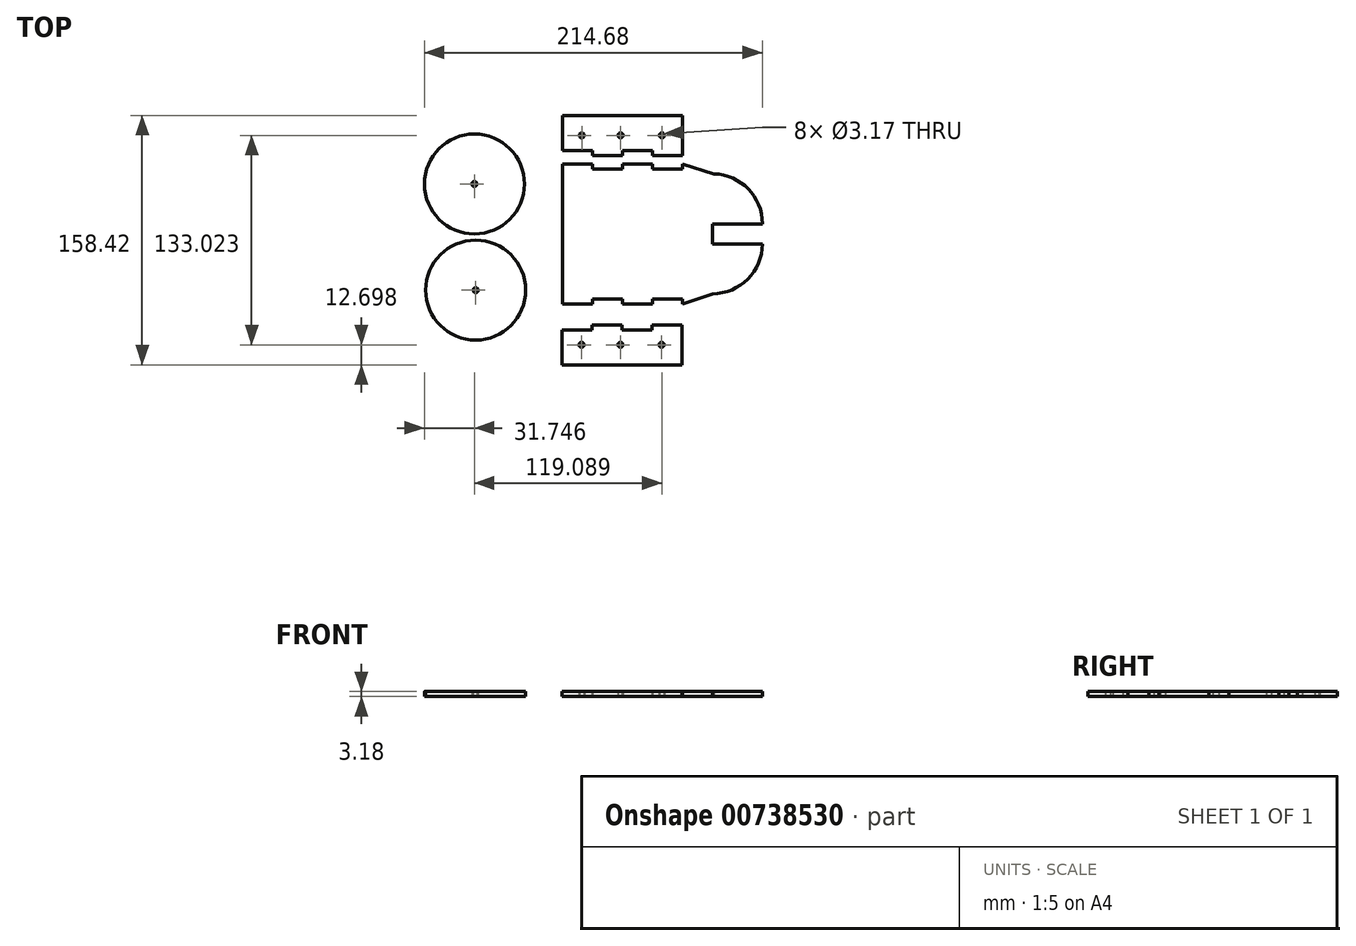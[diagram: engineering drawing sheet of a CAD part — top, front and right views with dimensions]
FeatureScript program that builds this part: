
annotation { "Feature Type Name" : "Feature", "Feature Type Description" : "" }
export const myFeature = defineFeature(function(context is Context, id is Id, definition is map)
    precondition{}
    {
        {
            var Q0;
            Q0=qCreatedBy(makeId("Top.planeOp"),FACE);
            var sketch = newSketch(context, id + "F0", { "sketchPlane" : qUnion([Q0])});
            skLineSegment(sketch, "E0.bottom", {"start": v(0, 0) * mm, "end": v(19.05, 0) * mm});
            skLineSegment(sketch, "E0.top", {"start": v(0, 88.9) * mm, "end": v(19.05, 88.9) * mm});
            skLineSegment(sketch, "E0.left", {"start": v(0, 0) * mm, "end": v(0, 88.9) * mm});
            skLineSegment(sketch, "E1.top", {"start": v(19.05, 85.73) * mm, "end": v(38.1, 85.73) * mm});
            skLineSegment(sketch, "E1.left", {"start": v(19.05, 88.9) * mm, "end": v(19.05, 85.73) * mm});
            skLineSegment(sketch, "E1.right", {"start": v(38.1, 88.9) * mm, "end": v(38.1, 85.73) * mm});
            skLineSegment(sketch, "E2.top", {"start": v(57.15, 85.73) * mm, "end": v(76.2, 85.73) * mm});
            skLineSegment(sketch, "E2.left", {"start": v(57.15, 88.9) * mm, "end": v(57.15, 85.73) * mm});
            skLineSegment(sketch, "E2.right", {"start": v(76.2, 88.9) * mm, "end": v(76.2, 85.73) * mm});
            skLineSegment(sketch, "E3.top", {"start": v(19.05, 3.18) * mm, "end": v(38.1, 3.18) * mm});
            skLineSegment(sketch, "E3.left", {"start": v(19.05, 0) * mm, "end": v(19.05, 3.18) * mm});
            skLineSegment(sketch, "E3.right", {"start": v(38.1, 0) * mm, "end": v(38.1, 3.18) * mm});
            skLineSegment(sketch, "E4.top", {"start": v(57.15, 3.18) * mm, "end": v(76.2, 3.18) * mm});
            skLineSegment(sketch, "E4.left", {"start": v(57.15, 0) * mm, "end": v(57.15, 3.18) * mm});
            skLineSegment(sketch, "E4.right", {"start": v(76.2, 0) * mm, "end": v(76.2, 3.18) * mm});
            skLineSegment(sketch, "E5.bottom", {"start": v(19.05, 94.26) * mm, "end": v(38.1, 94.26) * mm});
            skLineSegment(sketch, "E5.top", {"start": v(0, 119.66) * mm, "end": v(50.8, 119.66) * mm});
            skLineSegment(sketch, "E5.left", {"start": v(0, 97.44) * mm, "end": v(0, 119.66) * mm});
            skLineSegment(sketch, "E5.right", {"start": v(76.2, 123.98) * mm, "end": v(76.2, 123.98) * mm});
            skLineSegment(sketch, "E6.top", {"start": v(0, 97.44) * mm, "end": v(19.05, 97.44) * mm});
            skLineSegment(sketch, "E6.right", {"start": v(19.05, 94.26) * mm, "end": v(19.05, 97.44) * mm});
            skLineSegment(sketch, "E7.top", {"start": v(38.1, 97.44) * mm, "end": v(57.15, 97.44) * mm});
            skLineSegment(sketch, "E7.left", {"start": v(38.1, 94.26) * mm, "end": v(38.1, 97.44) * mm});
            skLineSegment(sketch, "E7.right", {"start": v(57.15, 94.26) * mm, "end": v(57.15, 97.44) * mm});
            skLineSegment(sketch, "E8.trimOffspring", {"start": v(57.15, 94.26) * mm, "end": v(76.2, 94.26) * mm});
            skPoint(sketch, "E9.orphan", {"position": v(0, 94.26) * mm});
            skLineSegment(sketch, "E10.trimOffspring", {"start": v(38.1, 88.9) * mm, "end": v(57.15, 88.9) * mm});
            skLineSegment(sketch, "E11.trimOffspring", {"start": v(38.1, 0) * mm, "end": v(57.15, 0) * mm});
            skLineSegment(sketch, "E12.bottom", {"start": v(127, 50.8) * mm, "end": v(95.25, 50.8) * mm});
            skLineSegment(sketch, "E12.top", {"start": v(127, 38.1) * mm, "end": v(95.25, 38.1) * mm});
            skLineSegment(sketch, "E12.right", {"start": v(95.25, 50.8) * mm, "end": v(95.25, 38.1) * mm});
            skPoint(sketch, "E13.1.internal.orphan", {"position": v(115.41, 11.02) * mm});
            skPoint(sketch, "E14.1.internal.orphan", {"position": v(115.41, 74.92) * mm});
            skArc(sketch, "E15", {"start": v(127, 50.8) * mm, "mid": v(118.02, 72.93) * mm, "end": v(96.15, 82.54) * mm});
            skArc(sketch, "E16", {"start": v(127, 38.1) * mm, "mid": v(117.7, 15.65) * mm, "end": v(95.25, 6.35) * mm});
            skLineSegment(sketch, "E17", {"start": v(76.2, 0) * mm, "end": v(95.25, 6.35) * mm});
            skLineSegment(sketch, "E18", {"start": v(96.15, 82.54) * mm, "end": v(76.2, 88.9) * mm});
            skPoint(sketch, "E19.visualSharp", {"position": v(76.2, 119.66) * mm});
            skCircle(sketch, "E20", {"center": v(12.27, 106.96) * mm, "radius": 1.59 * mm});
            skCircle(sketch, "E21", {"center": v(36.96, 106.96) * mm, "radius": 1.59 * mm});
            skCircle(sketch, "E22", {"center": v(63.15, 106.96) * mm, "radius": 1.59 * mm});
            skLineSegment(sketch, "E23", {"start": v(50.8, 119.66) * mm, "end": v(76.2, 119.66) * mm});
            skLineSegment(sketch, "E24", {"start": v(76.2, 119.66) * mm, "end": v(76.2, 94.26) * mm});
            skCircle(sketch, "E25", {"center": v(-55.93, 76.1) * mm, "radius": 31.75 * mm});
            skCircle(sketch, "E26", {"center": v(-55.93, 76.1) * mm, "radius": 1.59 * mm});
            skCircle(sketch, "E27", {"center": v(-55.09, 8.68) * mm, "radius": 31.75 * mm});
            skCircle(sketch, "E28", {"center": v(-55.09, 8.68) * mm, "radius": 1.59 * mm});
            skLineSegment(sketch, "E29.left", {"start": v(-0.16, -16.54) * mm, "end": v(-0.16, -38.76) * mm});
            skPoint(sketch, "E30.orphan", {"position": v(-0.16, -13.36) * mm});
            skLineSegment(sketch, "E31.MirrorCS", {"start": v(18.9, -13.36) * mm, "end": v(18.9, -16.54) * mm});
            skLineSegment(sketch, "E32.MirrorCS", {"start": v(57, -13.36) * mm, "end": v(57, -16.54) * mm});
            skLineSegment(sketch, "E33.MirrorCS", {"start": v(37.94, -13.36) * mm, "end": v(37.94, -16.54) * mm});
            skCircle(sketch, "E34.MirrorC", {"center": v(63, -26.06) * mm, "radius": 1.59 * mm});
            skLineSegment(sketch, "E35.MirrorCS", {"start": v(76.04, -13.36) * mm, "end": v(76.04, -38.76) * mm});
            skLineSegment(sketch, "E36.MirrorCS", {"start": v(57, -13.36) * mm, "end": v(76.04, -13.36) * mm});
            skLineSegment(sketch, "E37.MirrorCS", {"start": v(-0.16, -16.54) * mm, "end": v(18.9, -16.54) * mm});
            skLineSegment(sketch, "E38.MirrorCS", {"start": v(36.84, -38.76) * mm, "end": v(76.04, -38.76) * mm});
            skLineSegment(sketch, "E39.MirrorCS", {"start": v(76.04, -38.76) * mm, "end": v(76.04, -13.36) * mm});
            skCircle(sketch, "E40.MirrorC", {"center": v(12.11, -26.06) * mm, "radius": 1.59 * mm});
            skPoint(sketch, "E41.MirrorP", {"position": v(76.04, -38.76) * mm});
            skLineSegment(sketch, "E42.MirrorCS", {"start": v(37.94, -16.54) * mm, "end": v(57, -16.54) * mm});
            skLineSegment(sketch, "E43.MirrorCS", {"start": v(-0.16, -38.76) * mm, "end": v(36.84, -38.76) * mm});
            skLineSegment(sketch, "E44.MirrorCS", {"start": v(18.9, -13.36) * mm, "end": v(37.94, -13.36) * mm});
            skCircle(sketch, "E45.MirrorC", {"center": v(36.8, -26.06) * mm, "radius": 1.59 * mm});
            skSolve(sketch);
        }
        {
            var Q0;
            Q0=makeQuery(id+"F0.imprint","IMPRINT",FACE,{"disambiguationData":[TD([[makeQuery(id+"F0.imprint","IMPRINT",EDGE,{"derivedFrom":sQuery(id+"F0.wireOp",EDGE,"E5.bottom")}),1.0]])]});
            var Q1;
            Q1=makeQuery(id+"F0.imprint","IMPRINT",FACE,{"disambiguationData":[TD([[makeQuery(id+"F0.imprint","IMPRINT",EDGE,{"derivedFrom":sQuery(id+"F0.wireOp",EDGE,"E0.bottom")}),1.0]])]});
            var Q2;
            Q2=makeQuery(id+"F0.imprint","IMPRINT",FACE,{"disambiguationData":[TD([[makeQuery(id+"F0.imprint","IMPRINT",EDGE,{"derivedFrom":sQuery(id+"F0.wireOp",EDGE,"0dLW2gVW-DOgX-AZjm-PuBm-TPdizjULYMIW.bottom")}),-1.0]])]});
            var Q3;
            Q3=makeQuery(id+"F0.imprint","IMPRINT",FACE,{"disambiguationData":[TD([[makeQuery(id+"F0.imprint","IMPRINT",EDGE,{"derivedFrom":sQuery(id+"F0.wireOp",EDGE,"E25")}),1.0]])]});
            var Q4;
            Q4=makeQuery(id+"F0.imprint","IMPRINT",FACE,{"disambiguationData":[TD([[makeQuery(id+"F0.imprint","IMPRINT",EDGE,{"derivedFrom":sQuery(id+"F0.wireOp",EDGE,"E27")}),1.0]])]});
            var Q5;
            Q5=makeQuery(id+"F0.imprint","IMPRINT",FACE,{"disambiguationData":[TD([[makeQuery(id+"F0.imprint","IMPRINT",EDGE,{"derivedFrom":sQuery(id+"F0.wireOp",EDGE,"E29.left")}),1.0]])]});
            extrude(context, id + "F1", {"entities" : qUnion([Q0, Q1, Q2, Q3, Q4, Q5]), "depth" : 3.17 * mm, "offsetDistance" : 25.4 * mm});
        }
    });
